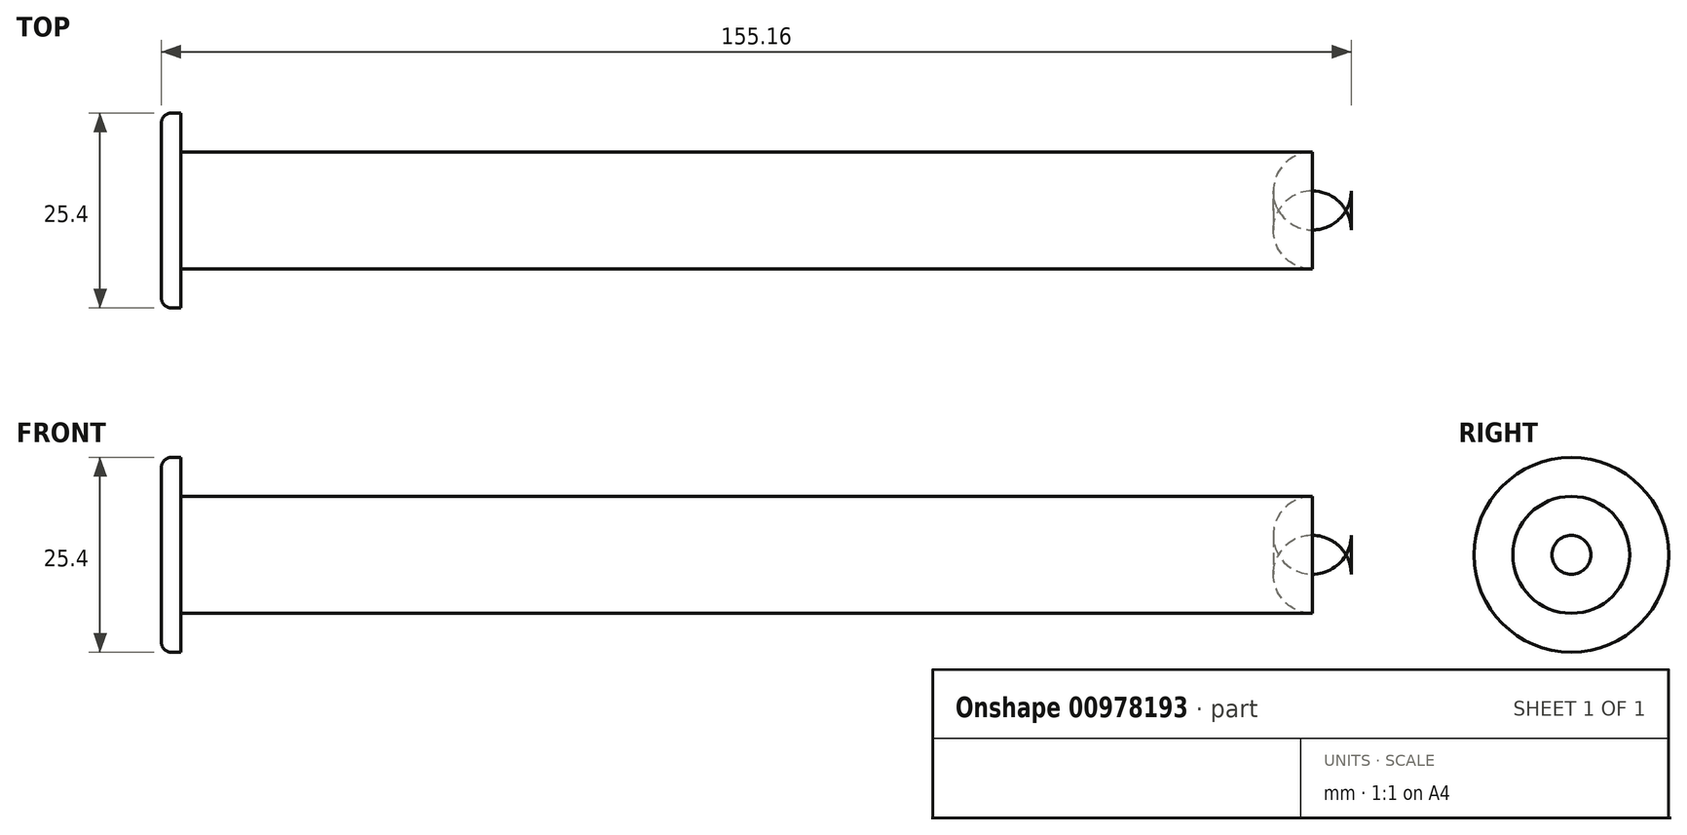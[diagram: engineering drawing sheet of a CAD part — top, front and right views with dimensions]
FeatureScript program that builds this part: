
annotation { "Feature Type Name" : "Feature", "Feature Type Description" : "" }
export const myFeature = defineFeature(function(context is Context, id is Id, definition is map)
    precondition{}
    {
        {
            var Q0;
            Q0=qCreatedBy(makeId("Top.planeOp"),FACE);
            var sketch = newSketch(context, id + "F0", { "sketchPlane" : qUnion([Q0])});
            skLineSegment(sketch, "E0", {"start": v(-96.64, 0) * mm, "end": v(55.98, 0) * mm});
            skLineSegment(sketch, "E1", {"start": v(55.98, 0) * mm, "end": v(55.98, 7.62) * mm});
            skLineSegment(sketch, "E2", {"start": v(55.98, 7.62) * mm, "end": v(-96.64, 7.62) * mm});
            skLineSegment(sketch, "E3", {"start": v(-96.64, 7.62) * mm, "end": v(-96.64, 0) * mm});
            skSolve(sketch);
        }
        {
            var Q0;
            Q0=makeQuery(id+"F0.imprint","IMPRINT",FACE,{"disambiguationData":[TD([[makeQuery(id+"F0.imprint","IMPRINT",EDGE,{"derivedFrom":sQuery(id+"F0.wireOp",EDGE,"E0")}),1.0]])]});
            var Q1;
            Q1=sQuery(id+"F0.wireOp",EDGE,"E0");
            revolve(context, id + "F1", {"surfaceOperationType" : NewSurfaceOperationType.NEW, "entities" : qUnion([Q0]), "axis" : qUnion([Q1]), "revolveType" : RevolveType.FULL});
        }
        {
            var Q0;
            Q0=makeQuery(id+"F1.opRevolve","SWEPT_EDGE",EDGE,{"disambiguationData":[OSD([sQuery(id+"F0.wireOp",EDGE,"E1"),sQuery(id+"F0.wireOp",EDGE,"E2")])]});
            fillet(context, id + "F2", {"entities" : qUnion([Q0]), "radius" : 5.08 * mm, "tangentPropagation" : true, "allowEdgeOverflow" : false});
        }
        {
            var Q0;
            Q0=makeQuery(id+"F1.opRevolve","SWEPT_FACE",FACE,{"disambiguationData":[OSD([sQuery(id+"F0.wireOp",EDGE,"E3")])]});
            var sketch = newSketch(context, id + "F3", { "sketchPlane" : qUnion([Q0])});
            skCircle(sketch, "E4", {"center": v(0, 0) * mm, "radius": 12.7 * mm});
            skSolve(sketch);
        }
        {
            var Q0;
            Q0 = qSketchRegion(id + "F3", true);
            extrude(context, id + "F4", {"entities" : qUnion([Q0]), "operationType" : NewBodyOperationType.ADD, "depth" : 2.54 * mm, "offsetDistance" : 25.4 * mm});
        }
        {
            var Q0;
            Q0=makeQuery(id+"F4.opExtrude","CAP_EDGE",EDGE,{"disambiguationData":[OSD([sQuery(id+"F3.wireOp",EDGE,"E4")])],"isStart":false});
            var Q1;
            Q1=makeQuery(id+"F1.opRevolve","SWEPT_EDGE",EDGE,{"disambiguationData":[OSD([sQuery(id+"F0.wireOp",EDGE,"E2"),sQuery(id+"F0.wireOp",EDGE,"E3")])]});
            fillet(context, id + "F5", {"entities" : qUnion([Q0, Q1]), "radius" : 1.27 * mm, "tangentPropagation" : true, "allowEdgeOverflow" : false});
        }
    });
